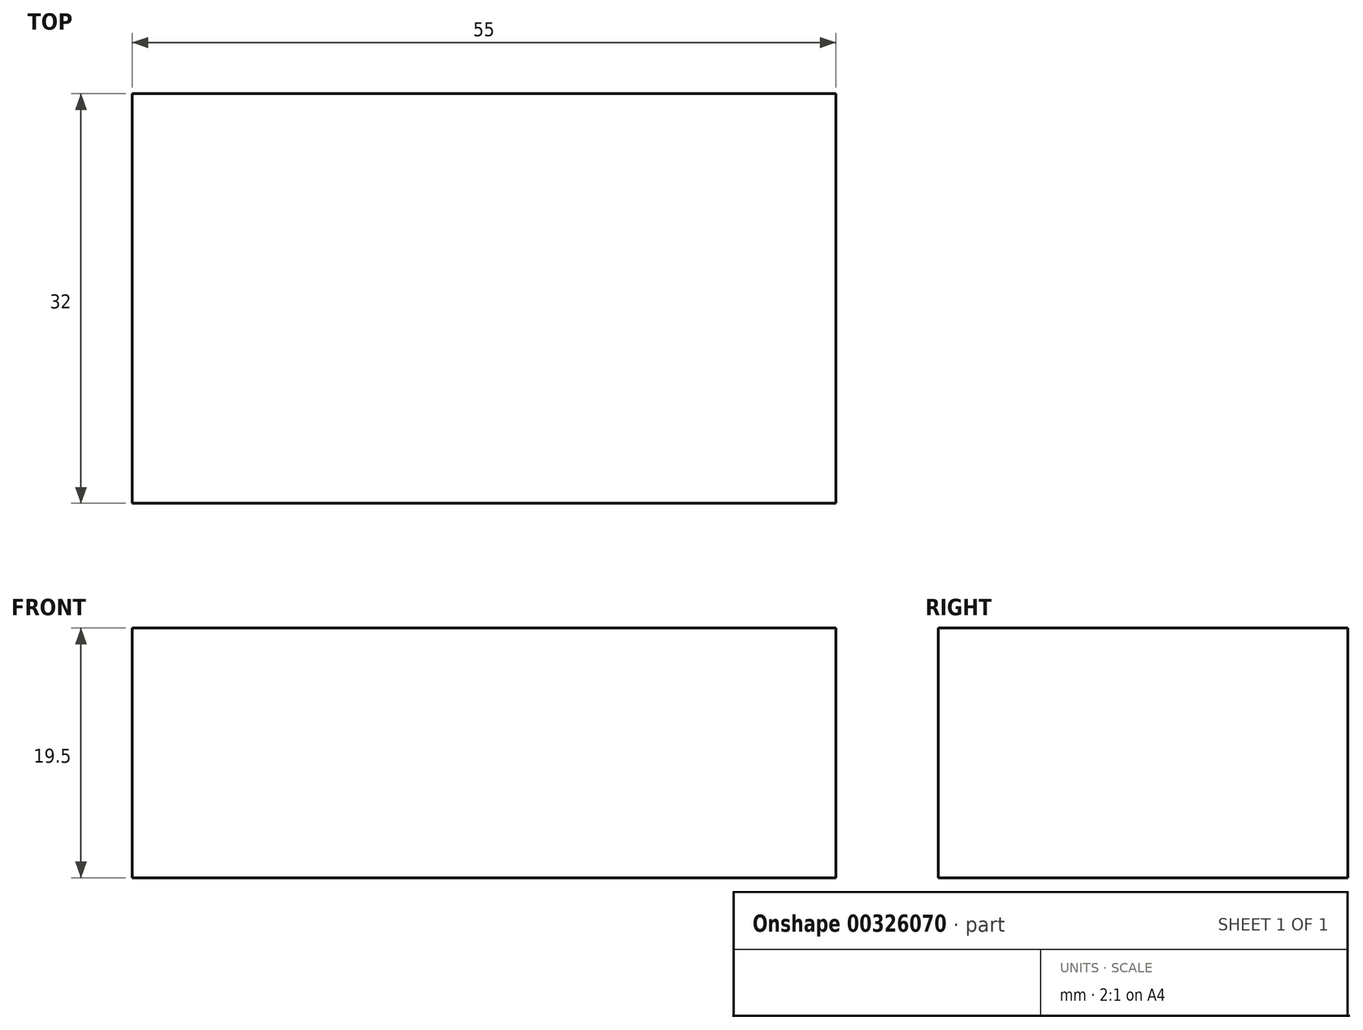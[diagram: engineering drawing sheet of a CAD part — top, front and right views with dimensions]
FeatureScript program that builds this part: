
annotation { "Feature Type Name" : "Feature", "Feature Type Description" : "" }
export const myFeature = defineFeature(function(context is Context, id is Id, definition is map)
    precondition{}
    {
        {
            var Q0;
            Q0=qCreatedBy(makeId("Top.planeOp"),FACE);
            var sketch = newSketch(context, id + "F0", { "sketchPlane" : qUnion([Q0])});
            skLineSegment(sketch, "E0.bottom", {"start": v(27.5, 16) * mm, "end": v(-27.5, 16) * mm});
            skLineSegment(sketch, "E0.top", {"start": v(27.5, -16) * mm, "end": v(-27.5, -16) * mm});
            skLineSegment(sketch, "E0.left", {"start": v(27.5, 16) * mm, "end": v(27.5, -16) * mm});
            skLineSegment(sketch, "E0.right", {"start": v(-27.5, 16) * mm, "end": v(-27.5, -16) * mm});
            skPoint(sketch, "E0.middle", {"position": v(0, 0) * mm});
            skSolve(sketch);
        }
        {
            var Q0;
            Q0 = qSketchRegion(id + "F0", true);
            extrude(context, id + "F1", {"entities" : qUnion([Q0]), "depth" : 19.5 * mm});
        }
    });
